# Revit family: QF_Culinaire_Refrigerated Cold Well_CR.CWCF.U.GSF.3_ CR.CWCF.U.GSF.8
name_source: partatom
category: Specialty Equipment
revit_build: Autodesk Revit Architecture 2014 (Build: 20140709_2115(x64)
units: mm (PartAtom-declared; Revit-internal decimal feet)

## types (6) — shared parameters
Assembly Code = E1090300
Body = QF_Stainless-Polished
Centre Section = QF_Stainless-Polished
Conn Plug = 10A plug & lead fitted
Control Panel = QF_Plastic-Black-Coarse
Depth = 825 mm  [stored 2.70669 ft]
Gantry = QF_Glass
Gantry Width = 809 mm  [stored 2.6542 ft]
Height = 1095 mm  [stored 3.59252 ft]
Manufacturer = Culinaire
Normal Operating Range = +2ºC to +4ºC in 32ºC ambient temperature
Phase = 1
Type Comments = This display is designed to be installed into a cut out in a new or existing bench top which allows for simple, inexpensive installation
URL = http://www.stoddart.com.au
Volts = 240 V

## per-type parameters (varying)
| type | Description | Number of Grill | Spacing of Grill | Watts | Width |
| CR.CWCF.U.GSF.3 | Refrigerated Well Counter Line_Under Bench_3 Modules | 2 | 346 mm | 820 W | 1285 mm  [stored 4.21588 ft] |
| CR.CWCF.U.GSF.4 | Refrigerated Well Counter Line_Under Bench_4 Modules | 3 | 344 mm | 820 W | 1625 mm  [stored 5.33136 ft] |
| CR.CWCF.U.GSF.5 | Refrigerated Well Counter Line_Under Bench_5 Modules | 4 | 343 mm | 900 W | 1965 mm  [stored 6.44685 ft] |
| CR.CWCF.U.GSF.6 | Refrigerated Well Counter Line_Under Bench_6 Modules | 5 | 343 mm | 900 W | 2305 mm  [stored 7.56234 ft] |
| CR.CWCF.U.GSF.7 | Refrigerated Well Counter Line_Under Bench_7 Modules | 6 | 342 mm | 1200 W | 2645 mm  [stored 8.67782 ft] |
| CR.CWCF.U.GSF.8 | Refrigerated Well Counter Line_Under Bench_8 Modules | 7 | 342 mm | 1200 W | 2985 mm  [stored 9.79331 ft] |

note: column(s) folded — value = type name in every type: Model

note: [stored X ft] marks values corroborated as IEEE doubles in the binary element streams (Revit-internal decimal feet)

## geometry (parser evidence)
native form markers: Sweep x6
no freeform markers — native parametric forms only
